# Revit family: 265-91-001 DN200_PN16
name_source: partatom
category: Pipe Accessories
units: mm (PartAtom-declared; Revit-internal decimal feet)

## family parameters
Always vertical = Yes
Cut with Voids When Loaded = No
Part Type = Valve - Breaks Into
Round Connector Dimension = Use Diameter
Shared = No
Work Plane-Based = No

## types (1)
- DN200_PN16
    25 = 25 mm  [stored 0.082021 ft]
    B1 = 29 mm
    Bolt.no = 12 mm  [stored 0.0393701 ft]
    Bore = 100 mm  [stored 0.328084 ft]
    D = 170 mm  [stored 0.557743 ft]
    DN = 200 mm  [stored 0.656168 ft]
    DN200_PN16 = 265-9-0200-10-14036400
    Default Elevation = 0 mm  [stored 0 ft]
    Description_ = AVK DISMANTLING JOINT WITH CENTRE FLANGE, PN10/16
    FL_T = 20 mm  [stored 0.0656168 ft]
    FL_T/2 = 10 mm  [stored 0.0328084 ft]
    L = 360 mm  [stored 1.1811 ft]
    L1 = 150 mm  [stored 0.492126 ft]
    L11 = 220 mm  [stored 0.721785 ft]
    L2 = 23 mm
    L3 = 10 mm  [stored 0.0328084 ft]
    Nut_T = 15 mm  [stored 0.0492126 ft]
    PCD = 148 mm
    PN = 16 mm  [stored 0.0524934 ft]
    Raised_dis = 3 mm  [stored 0.00984252 ft]
    S = 20 mm  [stored 0.0656168 ft]
    S11 = 27 mm  [stored 0.0885827 ft]
    Search_table = 265-91-001 DN200_PN16
    T = 6 mm  [stored 0.019685 ft]
    T1 = 15 mm  [stored 0.0492126 ft]
    URL_product_pages = https://www.avkvalves.com
    offset = 7 mm  [stored 0.0229659 ft]
    raised_R = 128 mm

note: [stored X ft] marks values corroborated as IEEE doubles in the binary element streams (Revit-internal decimal feet)

## geometry (parser evidence)
native form markers: Sweep x16
no freeform markers — native parametric forms only
